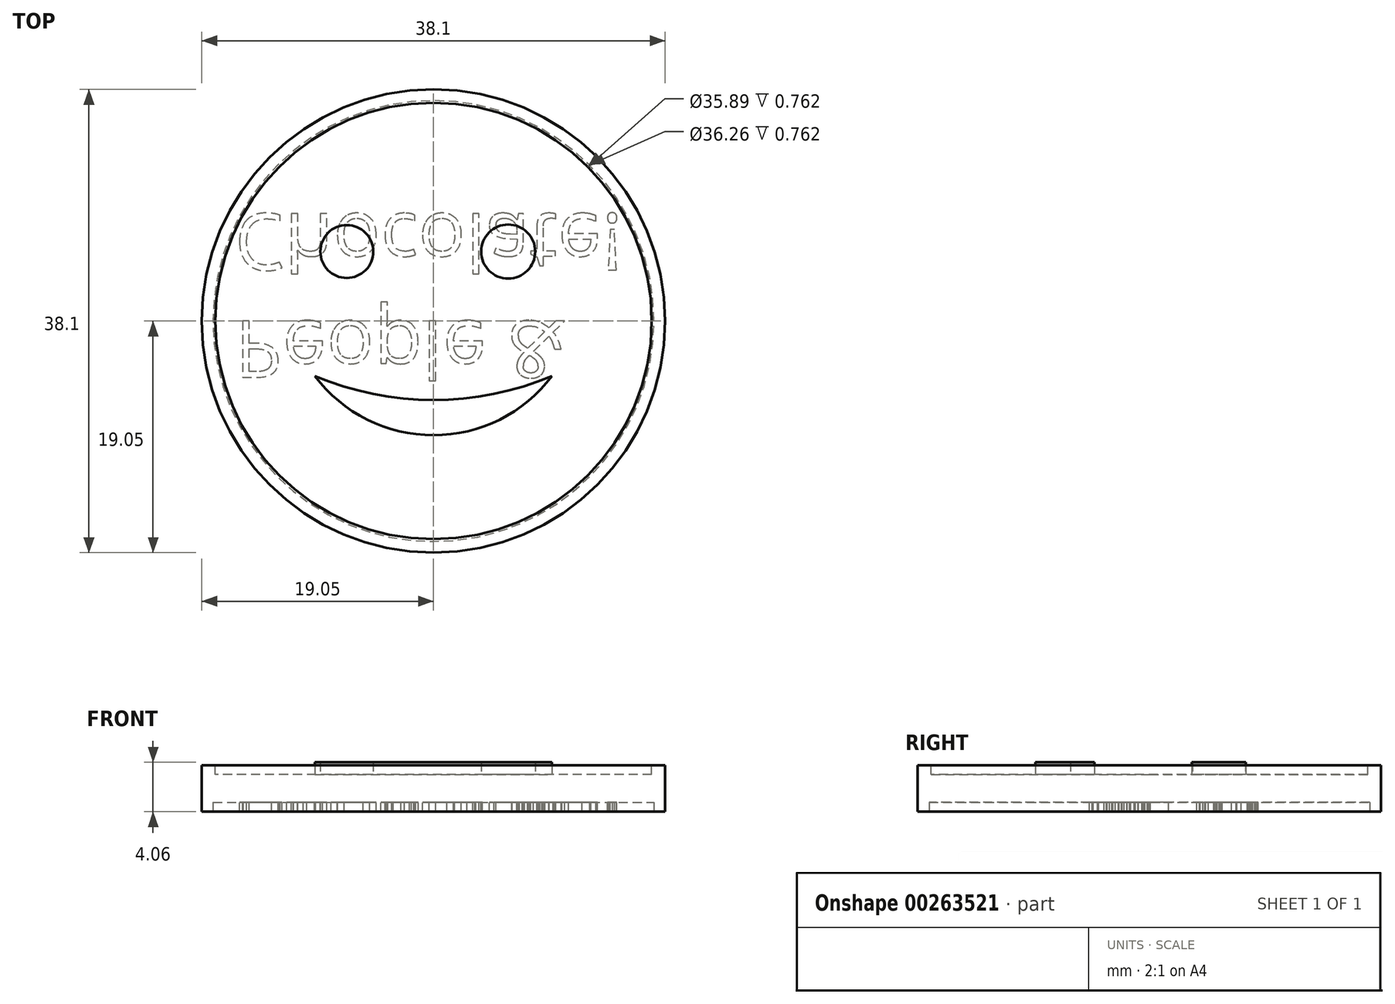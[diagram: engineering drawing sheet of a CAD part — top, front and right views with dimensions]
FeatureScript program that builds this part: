
annotation { "Feature Type Name" : "Feature", "Feature Type Description" : "" }
export const myFeature = defineFeature(function(context is Context, id is Id, definition is map)
    precondition{}
    {
        {
            var Q0;
            Q0=qCreatedBy(makeId("Top.planeOp"),FACE);
            var sketch = newSketch(context, id + "F0", { "sketchPlane" : qUnion([Q0])});
            skCircle(sketch, "E0", {"center": v(0, 0) * mm, "radius": 19.05 * mm});
            skSolve(sketch);
        }
        {
            var Q0;
            Q0 = qSketchRegion(id + "F0", true);
            extrude(context, id + "F1", {"entities" : qUnion([Q0]), "depth" : 3.8 * mm});
        }
        {
            var Q0;
            Q0=makeQuery(id+"F1.opExtrude","CAP_FACE",FACE,{"disambiguationData":[OSD([sQuery(id+"F0.wireOp",EDGE,"E0")])],"isStart":false});
            var sketch = newSketch(context, id + "F2", { "sketchPlane" : qUnion([Q0])});
            skCircle(sketch, "E1", {"center": v(0, 0) * mm, "radius": 17.94 * mm});
            skSolve(sketch);
        }
        {
            var Q0;
            Q0=makeQuery(id+"F2.imprint","IMPRINT",FACE,{"disambiguationData":[TD([[makeQuery(id+"F2.imprint","IMPRINT",EDGE,{"derivedFrom":sQuery(id+"F2.wireOp",EDGE,"E1")}),1.0]])]});
            extrude(context, id + "F3", {"entities" : qUnion([Q0]), "operationType" : NewBodyOperationType.REMOVE, "oppositeDirection" : true, "depth" : 0.76 * mm});
        }
        {
            var Q0;
            Q0=makeQuery(id+"F3.boolean.opBoolean","COPY",FACE,{"derivedFrom":makeQuery(id+"F3.opExtrude","CAP_FACE",FACE,{"disambiguationData":[OSD([sQuery(id+"F2.wireOp",EDGE,"E1")])],"isStart":false})});
            var sketch = newSketch(context, id + "F4", { "sketchPlane" : qUnion([Q0])});
            skCircle(sketch, "E2", {"center": v(-7.13, 5.71) * mm, "radius": 2.17 * mm});
            skCircle(sketch, "E3", {"center": v(6.14, 5.71) * mm, "radius": 2.22 * mm});
            skArc(sketch, "E4", {"start": v(-9.75, -4.53) * mm, "mid": v(0, -9.4) * mm, "end": v(9.75, -4.53) * mm});
            skArc(sketch, "E5", {"start": v(-9.75, -4.53) * mm, "mid": v(0, -6.49) * mm, "end": v(9.75, -4.53) * mm});
            skSolve(sketch);
        }
        {
            var Q0;
            Q0=makeQuery(id+"F1.opExtrude","CAP_FACE",FACE,{"disambiguationData":[OSD([sQuery(id+"F0.wireOp",EDGE,"E0")])],"isStart":true});
            var sketch = newSketch(context, id + "F5", { "sketchPlane" : qUnion([Q0])});
            skCircle(sketch, "E6", {"center": v(0, 0) * mm, "radius": 18.13 * mm});
            skSolve(sketch);
        }
        {
            var Q0;
            Q0=makeQuery(id+"F5.imprint","IMPRINT",FACE,{"disambiguationData":[TD([[makeQuery(id+"F5.imprint","IMPRINT",EDGE,{"derivedFrom":sQuery(id+"F5.wireOp",EDGE,"E6")}),1.0]])]});
            extrude(context, id + "F6", {"entities" : qUnion([Q0]), "operationType" : NewBodyOperationType.REMOVE, "oppositeDirection" : true, "depth" : 0.76 * mm});
        }
        {
            var Q0;
            Q0=makeQuery(id+"F6.boolean.opBoolean","COPY",FACE,{"derivedFrom":makeQuery(id+"F6.opExtrude","CAP_FACE",FACE,{"disambiguationData":[OSD([sQuery(id+"F5.wireOp",EDGE,"E6")])],"isStart":false})});
            var sketch = newSketch(context, id + "F7", { "sketchPlane" : qUnion([Q0])});
            skText(sketch, "E7", { "text": "People &\nChocolate!", "fontName": "OpenSans-Regular.ttf"});
            const initialGuessF7  = {"E7": [-0.01634, 0, 1, 0, 0.00467]};
            skSetInitialGuess(sketch, initialGuessF7);
            skSolve(sketch);
        }
        {
            var Q0;
            Q0 = qSketchRegion(id + "F7", true);
            extrude(context, id + "F8", {"entities" : qUnion([Q0]), "operationType" : NewBodyOperationType.ADD, "depth" : 0.76 * mm});
        }
        {
            var Q0;
            Q0 = qSketchRegion(id + "F4", true);
            extrude(context, id + "F9", {"entities" : qUnion([Q0]), "operationType" : NewBodyOperationType.ADD, "depth" : 1.02 * mm});
        }
    });
